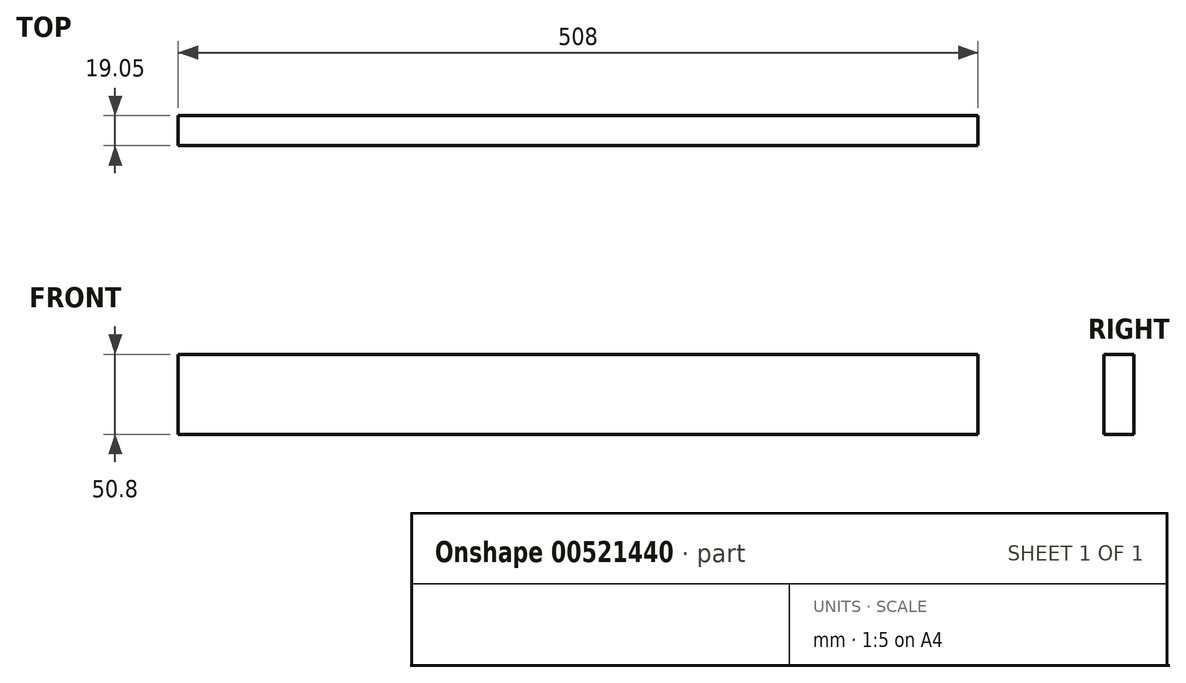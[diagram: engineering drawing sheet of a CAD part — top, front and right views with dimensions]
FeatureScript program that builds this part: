
annotation { "Feature Type Name" : "Feature", "Feature Type Description" : "" }
export const myFeature = defineFeature(function(context is Context, id is Id, definition is map)
    precondition{}
    {
        {
            var Q0;
            Q0=qCreatedBy(makeId("Top.planeOp"),FACE);
            var sketch = newSketch(context, id + "F0", { "sketchPlane" : qUnion([Q0])});
            skLineSegment(sketch, "E0.bottom", {"start": v(-253.72, -29.25) * mm, "end": v(254.28, -29.25) * mm});
            skLineSegment(sketch, "E0.top", {"start": v(-253.72, -48.3) * mm, "end": v(254.28, -48.3) * mm});
            skLineSegment(sketch, "E0.left", {"start": v(-253.72, -29.25) * mm, "end": v(-253.72, -48.3) * mm});
            skLineSegment(sketch, "E0.right", {"start": v(254.28, -29.25) * mm, "end": v(254.28, -48.3) * mm});
            skSolve(sketch);
        }
        {
            var Q0;
            Q0=makeQuery(id+"F0.imprint","IMPRINT",FACE,{"disambiguationData":[TD([[makeQuery(id+"F0.imprint","IMPRINT",EDGE,{"derivedFrom":sQuery(id+"F0.wireOp",EDGE,"E0.bottom")}),-1.0]])]});
            extrude(context, id + "F1", {"entities" : qUnion([Q0]), "depth" : 50.8 * mm, "offsetDistance" : 25.4 * mm});
        }
    });
